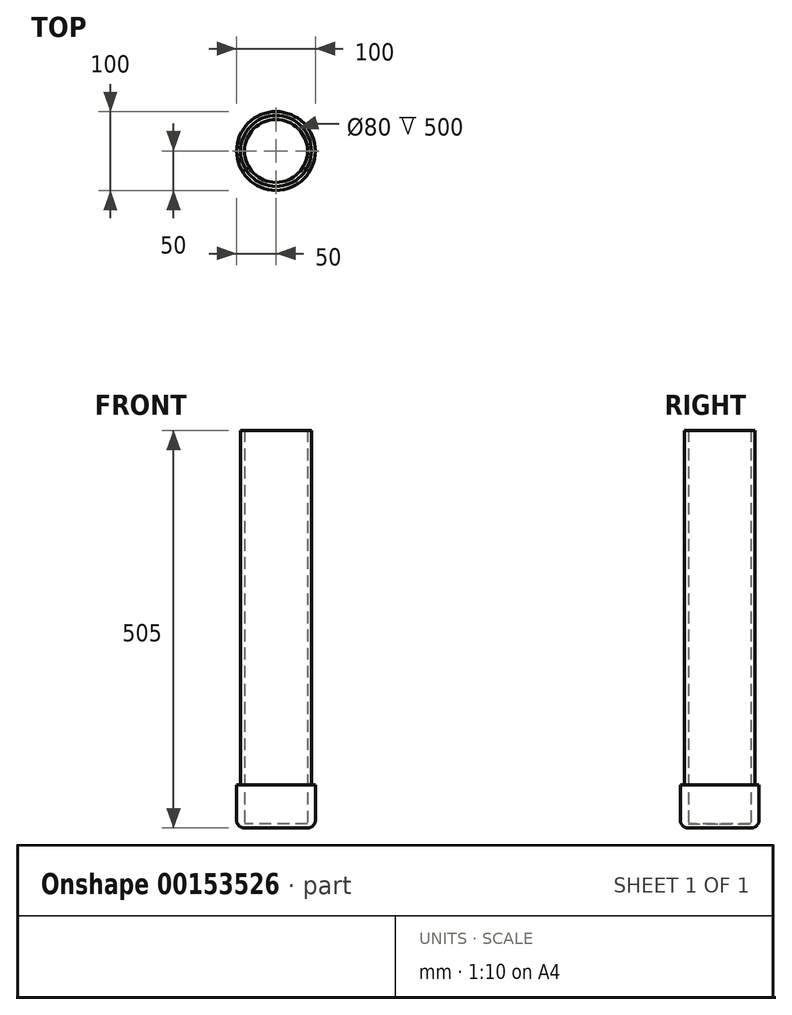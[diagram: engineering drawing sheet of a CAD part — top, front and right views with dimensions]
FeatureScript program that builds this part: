
annotation { "Feature Type Name" : "Feature", "Feature Type Description" : "" }
export const myFeature = defineFeature(function(context is Context, id is Id, definition is map)
    precondition{}
    {
        {
            var Q0;
            Q0=qCreatedBy(makeId("Top.planeOp"),FACE);
            var sketch = newSketch(context, id + "F0", { "sketchPlane" : qUnion([Q0])});
            skCircle(sketch, "E0", {"center": v(0, 0) * mm, "radius": 40 * mm});
            skCircle(sketch, "E1", {"center": v(0, 0) * mm, "radius": 45 * mm});
            skCircle(sketch, "E2", {"center": v(0, 0) * mm, "radius": 50 * mm});
            skSolve(sketch);
        }
        {
            var Q0;
            Q0=qSketchRegion(id+"F0",true);
            extrude(context, id + "F1", {"entities" : qUnion([Q0]), "depth" : 50 * mm});
        }
        {
            var Q0;
            Q0=makeQuery(id+"F0.imprint","IMPRINT",FACE,{"disambiguationData":[TD([[makeQuery(id+"F0.imprint","IMPRINT",EDGE,{"derivedFrom":sQuery(id+"F0.wireOp",EDGE,"E0")}),-1.0]])]});
            extrude(context, id + "F2", {"entities" : qUnion([Q0]), "operationType" : NewBodyOperationType.ADD, "depth" : 500 * mm});
        }
        {
            var Q0;
            Q0=makeQuery(id+"F0.imprint","IMPRINT",FACE,{"disambiguationData":[TD([[makeQuery(id+"F0.imprint","IMPRINT",EDGE,{"derivedFrom":sQuery(id+"F0.wireOp",EDGE,"E1")}),-1.0]])]});
            var Q1;
            Q1=makeQuery(id+"F0.imprint","IMPRINT",FACE,{"disambiguationData":[TD([[makeQuery(id+"F0.imprint","IMPRINT",EDGE,{"derivedFrom":sQuery(id+"F0.wireOp",EDGE,"E0")}),-1.0]])]});
            var Q2;
            Q2=makeQuery(id+"F0.imprint","IMPRINT",FACE,{"disambiguationData":[TD([[makeQuery(id+"F0.imprint","IMPRINT",EDGE,{"derivedFrom":sQuery(id+"F0.wireOp",EDGE,"E0")}),1.0]])]});
            extrude(context, id + "F3", {"entities" : qUnion([Q0, Q1, Q2]), "operationType" : NewBodyOperationType.ADD, "oppositeDirection" : true, "depth" : 5 * mm});
        }
        {
            var Q0;
            Q0=makeQuery(id+"F3.opExtrude","CAP_EDGE",EDGE,{"disambiguationData":[OSD([sQuery(id+"F0.wireOp",EDGE,"E2")])],"isStart":false});
            fillet(context, id + "F4", {"entities" : qUnion([Q0]), "radius" : 10 * mm, "tangentPropagation" : true, "allowEdgeOverflow" : false});
        }
    });
